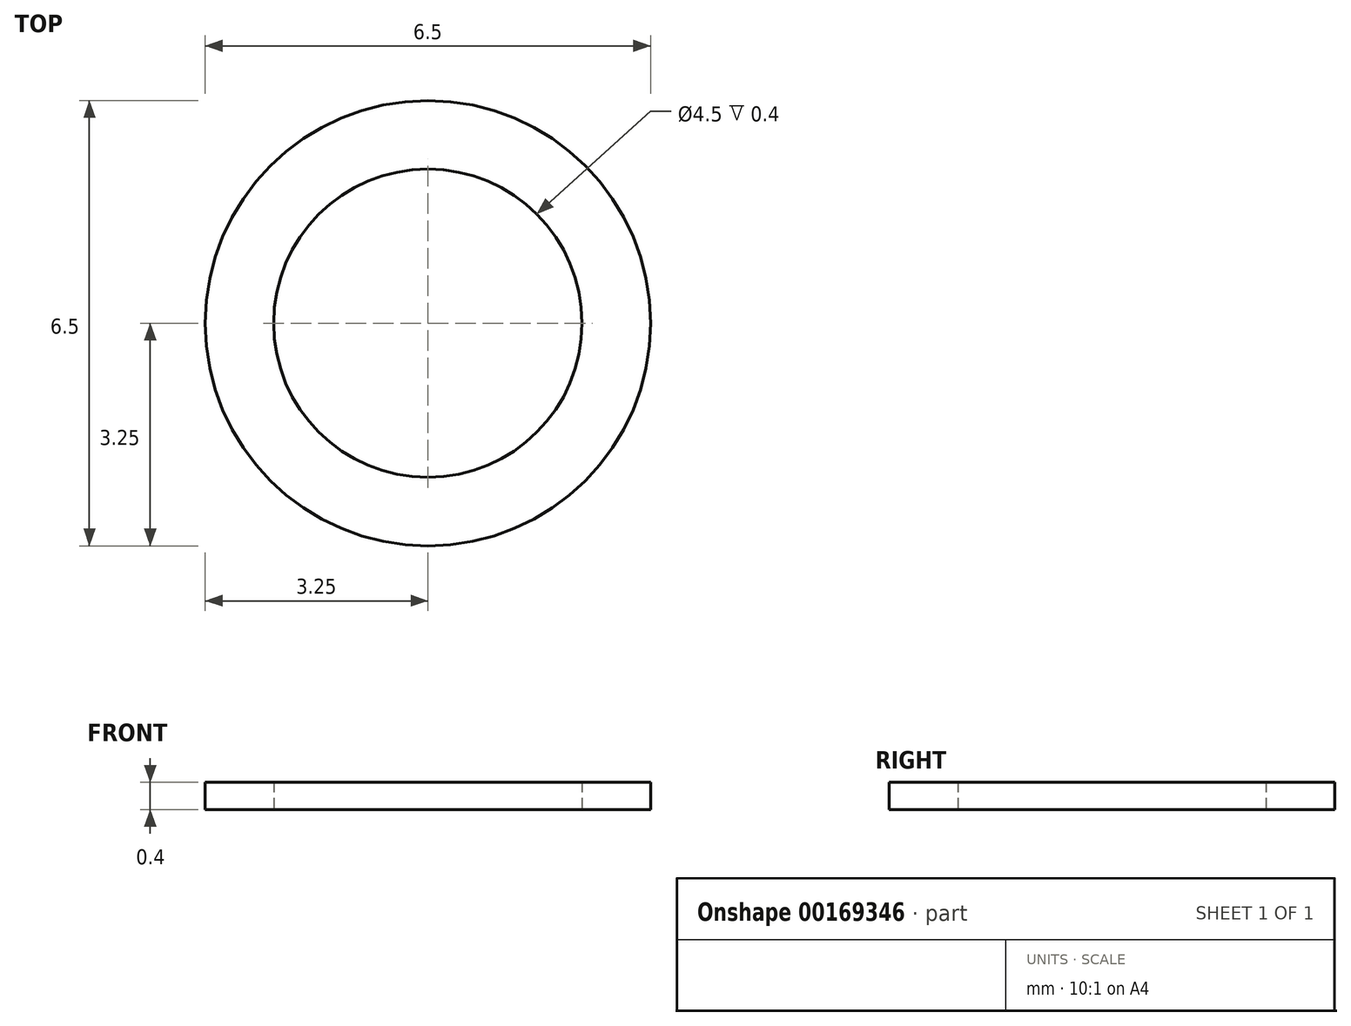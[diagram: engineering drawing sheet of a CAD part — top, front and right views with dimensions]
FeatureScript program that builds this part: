
annotation { "Feature Type Name" : "Feature", "Feature Type Description" : "" }
export const myFeature = defineFeature(function(context is Context, id is Id, definition is map)
    precondition{}
    {
        {
            var Q0;
            Q0=qCreatedBy(makeId("Top.planeOp"),FACE);
            var sketch = newSketch(context, id + "F0", { "sketchPlane" : qUnion([Q0])});
            skCircle(sketch, "E0", {"center": v(0, 0) * mm, "radius": 3.25 * mm});
            skCircle(sketch, "E1", {"center": v(0, 0) * mm, "radius": 2.25 * mm});
            skSolve(sketch);
        }
        {
            var Q0;
            Q0=makeQuery(id+"F0.imprint","IMPRINT",FACE,{"disambiguationData":[TD([[makeQuery(id+"F0.imprint","IMPRINT",EDGE,{"derivedFrom":sQuery(id+"F0.wireOp",EDGE,"E0")}),1.0]])]});
            extrude(context, id + "F1", {"entities" : qUnion([Q0]), "depth" : 0.4 * mm});
        }
    });
